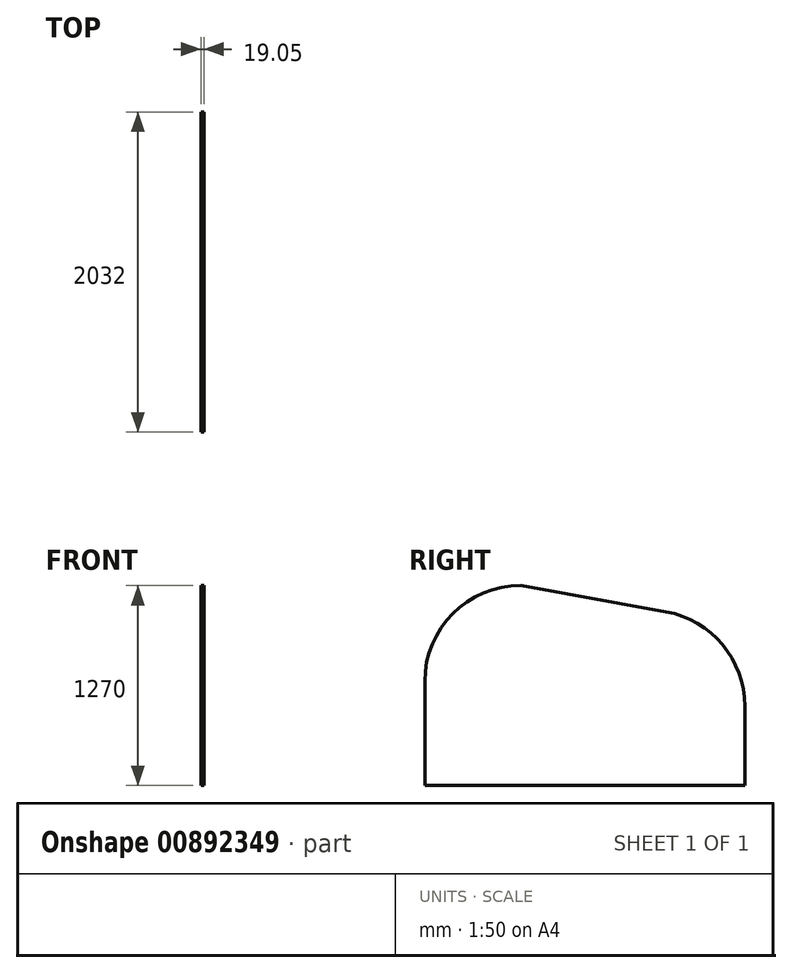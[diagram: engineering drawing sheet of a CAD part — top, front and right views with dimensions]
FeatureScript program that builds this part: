
annotation { "Feature Type Name" : "Feature", "Feature Type Description" : "" }
export const myFeature = defineFeature(function(context is Context, id is Id, definition is map)
    precondition{}
    {
        {
            var Q0;
            Q0=qCreatedBy(makeId("Right.planeOp"),FACE);
            var sketch = newSketch(context, id + "F0", { "sketchPlane" : qUnion([Q0])});
            skLineSegment(sketch, "E0", {"start": v(2032, 0) * mm, "end": v(0, 0) * mm, "construction": true});
            skLineSegment(sketch, "E1", {"start": v(0, 0) * mm, "end": v(0, 660.4) * mm, "construction": true});
            skLineSegment(sketch, "E2.top", {"start": v(0, 0) * mm, "end": v(2032, 0) * mm});
            skLineSegment(sketch, "E2.left", {"start": v(0, 660.4) * mm, "end": v(0, 0) * mm});
            skLineSegment(sketch, "E2.right", {"start": v(2032, 503.37) * mm, "end": v(2032, 0) * mm});
            skPoint(sketch, "E3.visualSharp", {"position": v(0, 1270) * mm});
            skArc(sketch, "E3.filletArc", {"start": v(609.6, 1270) * mm, "mid": v(178.55, 1091.45) * mm, "end": v(0, 660.4) * mm});
            skLineSegment(sketch, "E4", {"start": v(609.6, 1270) * mm, "end": v(1530.98, 1103.22) * mm});
            skPoint(sketch, "E5.visualSharp", {"position": v(2032, 1012.53) * mm});
            skArc(sketch, "E5.filletArc", {"start": v(2032, 503.37) * mm, "mid": v(1890.27, 894.15) * mm, "end": v(1530.98, 1103.22) * mm});
            skSolve(sketch);
        }
        {
            var Q0;
            Q0=makeQuery(id+"F0.imprint","IMPRINT",FACE,{"disambiguationData":[TD([[makeQuery(id+"F0.imprint","IMPRINT",EDGE,{"derivedFrom":sQuery(id+"F0.wireOp",EDGE,"E2.top")}),1.0]])]});
            extrude(context, id + "F1", {"entities" : qUnion([Q0]), "depth" : 19.05 * mm, "offsetDistance" : 25.4 * mm});
        }
    });
